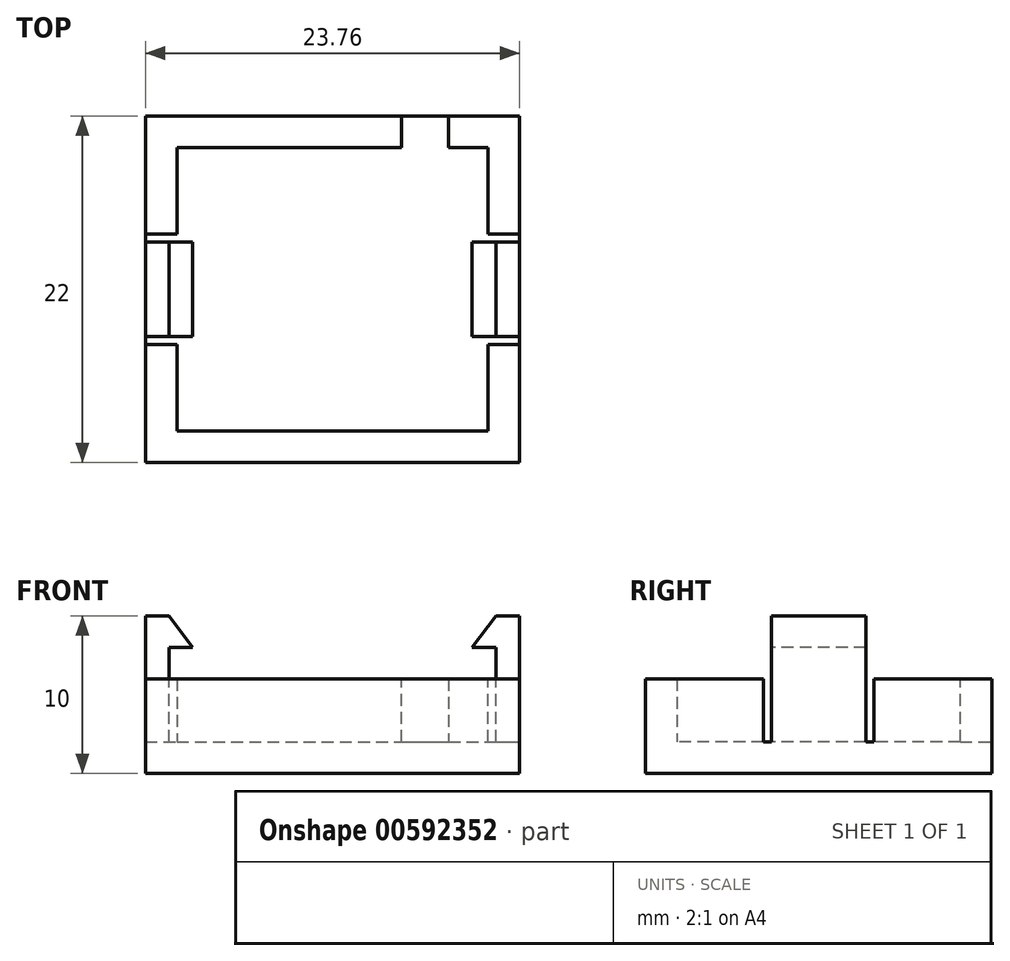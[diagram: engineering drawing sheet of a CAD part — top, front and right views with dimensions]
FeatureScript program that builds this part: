
annotation { "Feature Type Name" : "Feature", "Feature Type Description" : "" }
export const myFeature = defineFeature(function(context is Context, id is Id, definition is map)
    precondition{}
    {
        {
            var Q0;
            Q0=qCreatedBy(makeId("Top.planeOp"),FACE);
            var sketch = newSketch(context, id + "F0", { "sketchPlane" : qUnion([Q0])});
            skLineSegment(sketch, "E0.bottom", {"start": v(9.88, -9) * mm, "end": v(-9.88, -9) * mm});
            skLineSegment(sketch, "E0.top", {"start": v(9.88, 9) * mm, "end": v(-9.88, 9) * mm});
            skLineSegment(sketch, "E0.left", {"start": v(9.88, -9) * mm, "end": v(9.88, 9) * mm});
            skLineSegment(sketch, "E0.right", {"start": v(-9.88, -9) * mm, "end": v(-9.88, 9) * mm});
            skPoint(sketch, "E0.middle", {"position": v(0, 0) * mm});
            skLineSegment(sketch, "E1.bottom", {"start": v(11.88, -11) * mm, "end": v(-11.88, -11) * mm});
            skLineSegment(sketch, "E1.top", {"start": v(11.88, 11) * mm, "end": v(-11.88, 11) * mm});
            skLineSegment(sketch, "E1.left", {"start": v(11.88, -11) * mm, "end": v(11.88, 11) * mm});
            skLineSegment(sketch, "E1.right", {"start": v(-11.88, -11) * mm, "end": v(-11.88, 11) * mm});
            skSolve(sketch);
        }
        {
            var Q0;
            Q0 = qSketchRegion(id + "F0", true);
            var Q1;
            Q1=makeQuery(id+"F0.imprint","IMPRINT",FACE,{"disambiguationData":[TD([[makeQuery(id+"F0.imprint","IMPRINT",EDGE,{"derivedFrom":sQuery(id+"F0.wireOp",EDGE,"E0.bottom")}),-1.0]])]});
            extrude(context, id + "F1", {"entities" : qUnion([Q0, Q1]), "depth" : 2 * mm, "offsetDistance" : 25 * mm});
        }
        {
            var Q0;
            Q0=makeQuery(id+"F0.imprint","IMPRINT",FACE,{"disambiguationData":[TD([[makeQuery(id+"F0.imprint","IMPRINT",EDGE,{"derivedFrom":sQuery(id+"F0.wireOp",EDGE,"E0.bottom")}),1.0]])]});
            extrude(context, id + "F2", {"entities" : qUnion([Q0]), "operationType" : NewBodyOperationType.ADD, "depth" : 6 * mm, "offsetDistance" : 25 * mm});
        }
        {
            var Q0;
            Q0=makeQuery(id+"F2.opExtrude","CAP_FACE",FACE,{"disambiguationData":[OSD([sQuery(id+"F0.wireOp",EDGE,"E0.bottom"),sQuery(id+"F0.wireOp",EDGE,"E0.top"),sQuery(id+"F0.wireOp",EDGE,"E0.left"),sQuery(id+"F0.wireOp",EDGE,"E0.right"),sQuery(id+"F0.wireOp",EDGE,"E1.bottom"),sQuery(id+"F0.wireOp",EDGE,"E1.top"),sQuery(id+"F0.wireOp",EDGE,"E1.left"),sQuery(id+"F0.wireOp",EDGE,"E1.right")])],"isStart":false});
            var sketch = newSketch(context, id + "F3", { "sketchPlane" : qUnion([Q0])});
            skLineSegment(sketch, "E2.bottom", {"start": v(9.88, 3) * mm, "end": v(11.88, 3) * mm});
            skLineSegment(sketch, "E2.top", {"start": v(9.88, -3) * mm, "end": v(11.88, -3) * mm});
            skLineSegment(sketch, "E2.left", {"start": v(9.88, 3) * mm, "end": v(9.88, -3) * mm});
            skLineSegment(sketch, "E2.right", {"start": v(11.88, 3) * mm, "end": v(11.88, -3) * mm});
            skLineSegment(sketch, "E3", {"start": v(9.88, -3.5) * mm, "end": v(11.88, -3.5) * mm});
            skLineSegment(sketch, "E4", {"start": v(9.88, 3.5) * mm, "end": v(11.88, 3.5) * mm});
            skLineSegment(sketch, "E5", {"start": v(11.88, -3.5) * mm, "end": v(11.88, -3) * mm});
            skLineSegment(sketch, "E6", {"start": v(9.88, -3) * mm, "end": v(9.88, -3.5) * mm});
            skLineSegment(sketch, "E7", {"start": v(9.88, 3.5) * mm, "end": v(9.88, 3) * mm});
            skLineSegment(sketch, "E8", {"start": v(11.88, 3.5) * mm, "end": v(11.88, 3) * mm});
            skLineSegment(sketch, "E9.bottom", {"start": v(-11.88, 3) * mm, "end": v(-9.88, 3) * mm});
            skLineSegment(sketch, "E9.top", {"start": v(-11.88, -3) * mm, "end": v(-9.88, -3) * mm});
            skLineSegment(sketch, "E9.left", {"start": v(-11.88, 3) * mm, "end": v(-11.88, -3) * mm});
            skLineSegment(sketch, "E9.right", {"start": v(-9.88, 3) * mm, "end": v(-9.88, -3) * mm});
            skLineSegment(sketch, "E10.top", {"start": v(-11.88, 3.5) * mm, "end": v(-9.88, 3.5) * mm});
            skLineSegment(sketch, "E10.left", {"start": v(-11.88, 3) * mm, "end": v(-11.88, 3.5) * mm});
            skLineSegment(sketch, "E10.right", {"start": v(-9.88, 3) * mm, "end": v(-9.88, 3.5) * mm});
            skLineSegment(sketch, "E11.top", {"start": v(-11.88, -3.5) * mm, "end": v(-9.88, -3.5) * mm});
            skLineSegment(sketch, "E11.left", {"start": v(-11.88, -3) * mm, "end": v(-11.88, -3.5) * mm});
            skLineSegment(sketch, "E11.right", {"start": v(-9.88, -3) * mm, "end": v(-9.88, -3.5) * mm});
            skLineSegment(sketch, "E12.bottom", {"start": v(9.88, 3) * mm, "end": v(10.88, 3) * mm});
            skLineSegment(sketch, "E12.top", {"start": v(9.88, -3) * mm, "end": v(10.88, -3) * mm});
            skLineSegment(sketch, "E12.right", {"start": v(10.88, 3) * mm, "end": v(10.88, -3) * mm});
            skSolve(sketch);
        }
        {
            var Q0;
            Q0=makeQuery(id+"F3.imprint","IMPRINT",FACE,{"disambiguationData":[TD([[makeQuery(id+"F3.imprint","IMPRINT",EDGE,{"derivedFrom":sQuery(id+"F3.wireOp",EDGE,"E2.top")}),-1.0]])]});
            var Q1;
            Q1=makeQuery(id+"F3.imprint","IMPRINT",FACE,{"disambiguationData":[TD([[makeQuery(id+"F3.imprint","IMPRINT",EDGE,{"derivedFrom":sQuery(id+"F3.wireOp",EDGE,"E2.bottom")}),1.0]])]});
            var Q2;
            Q2=makeQuery(id+"F3.imprint","IMPRINT",FACE,{"disambiguationData":[TD([[makeQuery(id+"F3.imprint","IMPRINT",EDGE,{"derivedFrom":sQuery(id+"F3.wireOp",EDGE,"E9.bottom")}),1.0]])]});
            var Q3;
            Q3=makeQuery(id+"F3.imprint","IMPRINT",FACE,{"disambiguationData":[TD([[makeQuery(id+"F3.imprint","IMPRINT",EDGE,{"derivedFrom":sQuery(id+"F3.wireOp",EDGE,"E9.top")}),-1.0]])]});
            extrude(context, id + "F4", {"entities" : qUnion([Q0, Q1, Q2, Q3]), "operationType" : NewBodyOperationType.REMOVE, "oppositeDirection" : true, "depth" : 4 * mm, "offsetDistance" : 25 * mm});
        }
        {
            var Q0;
            {var subQ0=sQuery(id+"F0.wireOp",EDGE,"E0.left");var subQ1=sQuery(id+"F0.wireOp",EDGE,"E1.left");Q0=makeQuery(id+"F4.boolean.opBoolean","SPLIT",FACE,{"disambiguationData":[TD([makeQuery(id+"F4.opExtrude","SWEPT_FACE",FACE,{"disambiguationData":[OSD([sQuery(id+"F3.wireOp",EDGE,"E2.bottom")])]})])],"derivedFrom":makeQuery(id+"F2.opExtrude","CAP_FACE",FACE,{"disambiguationData":[OSD([sQuery(id+"F0.wireOp",EDGE,"E0.bottom"),sQuery(id+"F0.wireOp",EDGE,"E0.top"),subQ0,sQuery(id+"F0.wireOp",EDGE,"E0.right"),sQuery(id+"F0.wireOp",EDGE,"E1.bottom"),sQuery(id+"F0.wireOp",EDGE,"E1.top"),subQ1,sQuery(id+"F0.wireOp",EDGE,"E1.right")])],"isStart":false})});}
            var Q1;
            {var subQ0=sQuery(id+"F0.wireOp",EDGE,"E0.right");var subQ1=sQuery(id+"F0.wireOp",EDGE,"E1.right");Q1=makeQuery(id+"F4.boolean.opBoolean","SPLIT",FACE,{"disambiguationData":[TD([makeQuery(id+"F4.opExtrude","SWEPT_FACE",FACE,{"disambiguationData":[OSD([sQuery(id+"F3.wireOp",EDGE,"E9.bottom")])]})])],"derivedFrom":makeQuery(id+"F2.opExtrude","CAP_FACE",FACE,{"disambiguationData":[OSD([sQuery(id+"F0.wireOp",EDGE,"E0.bottom"),sQuery(id+"F0.wireOp",EDGE,"E0.top"),sQuery(id+"F0.wireOp",EDGE,"E0.left"),subQ0,sQuery(id+"F0.wireOp",EDGE,"E1.bottom"),sQuery(id+"F0.wireOp",EDGE,"E1.top"),sQuery(id+"F0.wireOp",EDGE,"E1.left"),subQ1])],"isStart":false})});}
            extrude(context, id + "F5", {"entities" : qUnion([Q0, Q1]), "operationType" : NewBodyOperationType.ADD, "depth" : 4 * mm, "offsetDistance" : 25 * mm});
        }
        {
            var Q0;
            {var subQ0=sQuery(id+"F3.wireOp",EDGE,"E2.top");Q0=makeQuery(id+"F5.boolean.opBoolean","MERGE",FACE,{"derivedFrom":[makeQuery(id+"F4.boolean.opBoolean","COPY",FACE,{"derivedFrom":makeQuery(id+"F4.opExtrude","SWEPT_FACE",FACE,{"disambiguationData":[OSD([subQ0])]})}),makeQuery(id+"F5.opExtrude","SWEPT_FACE",FACE,{"disambiguationData":[OSD([subQ0])]})]});}
            var sketch = newSketch(context, id + "F6", { "sketchPlane" : qUnion([Q0])});
            skLineSegment(sketch, "E13.bottom", {"start": v(11.88, 10) * mm, "end": v(10.38, 10) * mm});
            skLineSegment(sketch, "E13.top", {"start": v(11.88, 8) * mm, "end": v(10.38, 8) * mm});
            skLineSegment(sketch, "E13.left", {"start": v(11.88, 10) * mm, "end": v(11.88, 8) * mm});
            skLineSegment(sketch, "E13.right", {"start": v(10.38, 10) * mm, "end": v(10.38, 8) * mm});
            skLineSegment(sketch, "E14", {"start": v(10.37, 8) * mm, "end": v(11.87, 10) * mm});
            skLineSegment(sketch, "E15", {"start": v(10.38, 8) * mm, "end": v(-6.12, 8) * mm, "construction": true});
            skSolve(sketch);
        }
        {
            var Q0;
            {var subQ0=sQuery(id+"F6.wireOp",EDGE,"E13.top");Q0=makeQuery(id+"F6.imprint","IMPRINT",FACE,{"disambiguationData":[TD([[makeQuery(id+"F6.imprint","IMPRINT",EDGE,{"derivedFrom":subQ0}),-1.0]])]});}
            var Q1;
            {var subQ0=sQuery(id+"F6.wireOp",EDGE,"9DU1TNyU-t0Yq-bJ8T-y5l7-213zkWhciGSZ.top");Q1=makeQuery(id+"F6.imprint","IMPRINT",FACE,{"disambiguationData":[TD([[makeQuery(id+"F6.imprint","IMPRINT",EDGE,{"derivedFrom":subQ0}),1.0]])]});}
            extrude(context, id + "F7", {"entities" : qUnion([Q0, Q1]), "operationType" : NewBodyOperationType.ADD, "oppositeDirection" : true, "depth" : 6 * mm, "offsetDistance" : 25 * mm});
        }
        {
            var Q0;
            {var subQ0=sQuery(id+"F0.wireOp",EDGE,"E1.top");Q0=makeQuery(id+"F2.boolean.opBoolean","MERGE",FACE,{"derivedFrom":[makeQuery(id+"F1.opExtrude","SWEPT_FACE",FACE,{"disambiguationData":[OSD([subQ0])]}),makeQuery(id+"F2.opExtrude","SWEPT_FACE",FACE,{"disambiguationData":[OSD([subQ0])]})]});}
            var sketch = newSketch(context, id + "F8", { "sketchPlane" : qUnion([Q0])});
            skLineSegment(sketch, "E16.bottom", {"start": v(-4.38, 6) * mm, "end": v(-7.38, 6) * mm});
            skLineSegment(sketch, "E16.top", {"start": v(-4.38, 2) * mm, "end": v(-7.38, 2) * mm});
            skLineSegment(sketch, "E16.left", {"start": v(-4.38, 6) * mm, "end": v(-4.38, 2) * mm});
            skLineSegment(sketch, "E16.right", {"start": v(-7.38, 6) * mm, "end": v(-7.38, 2) * mm});
            skSolve(sketch);
        }
        {
            var Q0;
            Q0=makeQuery(id+"F8.imprint","IMPRINT",FACE,{"disambiguationData":[TD([[makeQuery(id+"F8.imprint","IMPRINT",EDGE,{"derivedFrom":sQuery(id+"F8.wireOp",EDGE,"E16.bottom")}),-1.0]])]});
            extrude(context, id + "F9", {"entities" : qUnion([Q0]), "operationType" : NewBodyOperationType.REMOVE, "oppositeDirection" : true, "depth" : 5.2 * mm, "offsetDistance" : 25 * mm});
        }
        {
            var Q0;
            {var subQ0=sQuery(id+"F0.wireOp",EDGE,"E0.right");var subQ1=sQuery(id+"F0.wireOp",EDGE,"E1.right");var subQ2=sQuery(id+"F0.wireOp",EDGE,"E1.left");var subQ3=sQuery(id+"F0.wireOp",EDGE,"E1.top");var subQ4=sQuery(id+"F0.wireOp",EDGE,"E1.bottom");var subQ5=sQuery(id+"F0.wireOp",EDGE,"E0.left");var subQ6=sQuery(id+"F0.wireOp",EDGE,"E0.top");var subQ7=sQuery(id+"F0.wireOp",EDGE,"E0.bottom");Q0=makeQuery(id+"F5.opExtrude","CAP_FACE",FACE,{"disambiguationData":[OSD([subQ7,subQ6,subQ5,subQ0,subQ4,subQ3,subQ2,subQ1]),TDD([makeQuery(id+"F4.boolean.opBoolean","SPLIT",FACE,{"disambiguationData":[TD([makeQuery(id+"F4.opExtrude","SWEPT_FACE",FACE,{"disambiguationData":[OSD([sQuery(id+"F3.wireOp",EDGE,"E9.bottom")])]})])],"derivedFrom":makeQuery(id+"F2.opExtrude","CAP_FACE",FACE,{"disambiguationData":[OSD([subQ7,subQ6,subQ5,subQ0,subQ4,subQ3,subQ2,subQ1])],"isStart":false})})])],"isStart":false});}
            var sketch = newSketch(context, id + "F10", { "sketchPlane" : qUnion([Q0])});
            skLineSegment(sketch, "E17.bottom", {"start": v(-9.88, 3) * mm, "end": v(-10.38, 3) * mm});
            skLineSegment(sketch, "E17.top", {"start": v(-9.88, -3) * mm, "end": v(-10.37, -3) * mm});
            skLineSegment(sketch, "E17.left", {"start": v(-9.88, 3) * mm, "end": v(-9.88, -3) * mm});
            skLineSegment(sketch, "E17.right", {"start": v(-10.38, 3) * mm, "end": v(-10.37, -3) * mm});
            skSolve(sketch);
        }
        {
            var Q0;
            Q0=makeQuery(id+"F10.imprint","IMPRINT",FACE,{"disambiguationData":[TD([[makeQuery(id+"F10.imprint","IMPRINT",EDGE,{"derivedFrom":sQuery(id+"F10.wireOp",EDGE,"E17.bottom")}),-1.0]])]});
            extrude(context, id + "F11", {"entities" : qUnion([Q0]), "operationType" : NewBodyOperationType.REMOVE, "oppositeDirection" : true, "depth" : 8 * mm, "offsetDistance" : 25 * mm});
        }
        {
            var Q0;
            {var subQ0=sQuery(id+"F0.wireOp",EDGE,"E0.left");var subQ1=sQuery(id+"F0.wireOp",EDGE,"E1.left");var subQ2=sQuery(id+"F0.wireOp",EDGE,"E1.right");var subQ3=sQuery(id+"F0.wireOp",EDGE,"E1.top");var subQ4=sQuery(id+"F0.wireOp",EDGE,"E1.bottom");var subQ5=sQuery(id+"F0.wireOp",EDGE,"E0.right");var subQ6=sQuery(id+"F0.wireOp",EDGE,"E0.top");var subQ7=sQuery(id+"F0.wireOp",EDGE,"E0.bottom");Q0=makeQuery(id+"F5.opExtrude","CAP_FACE",FACE,{"disambiguationData":[OSD([subQ7,subQ6,subQ0,subQ5,subQ4,subQ3,subQ1,subQ2]),TDD([makeQuery(id+"F4.boolean.opBoolean","SPLIT",FACE,{"disambiguationData":[TD([makeQuery(id+"F4.opExtrude","SWEPT_FACE",FACE,{"disambiguationData":[OSD([sQuery(id+"F3.wireOp",EDGE,"E2.bottom"),sQuery(id+"F3.wireOp",EDGE,"E12.bottom")])]})])],"derivedFrom":makeQuery(id+"F2.opExtrude","CAP_FACE",FACE,{"disambiguationData":[OSD([subQ7,subQ6,subQ0,subQ5,subQ4,subQ3,subQ1,subQ2])],"isStart":false})})])],"isStart":false});}
            var sketch = newSketch(context, id + "F12", { "sketchPlane" : qUnion([Q0])});
            skLineSegment(sketch, "E18.bottom", {"start": v(9.88, 3) * mm, "end": v(10.38, 3) * mm});
            skLineSegment(sketch, "E18.top", {"start": v(9.88, -3) * mm, "end": v(10.38, -3) * mm});
            skLineSegment(sketch, "E18.left", {"start": v(9.88, 3) * mm, "end": v(9.88, -3) * mm});
            skLineSegment(sketch, "E18.right", {"start": v(10.38, 3) * mm, "end": v(10.38, -3) * mm});
            skSolve(sketch);
        }
        {
            var Q0;
            Q0=makeQuery(id+"F12.imprint","IMPRINT",FACE,{"disambiguationData":[TD([[makeQuery(id+"F12.imprint","IMPRINT",EDGE,{"derivedFrom":sQuery(id+"F12.wireOp",EDGE,"E18.bottom")}),-1.0]])]});
            extrude(context, id + "F13", {"entities" : qUnion([Q0]), "operationType" : NewBodyOperationType.REMOVE, "oppositeDirection" : true, "depth" : 8 * mm, "offsetDistance" : 25 * mm});
        }
        {
            var Q0;
            {var subQ0=sQuery(id+"F3.wireOp",EDGE,"E12.top");var subQ1=sQuery(id+"F3.wireOp",EDGE,"E2.top");Q0=makeQuery(id+"F5.boolean.opBoolean","MERGE",FACE,{"derivedFrom":[makeQuery(id+"F4.boolean.opBoolean","COPY",FACE,{"derivedFrom":makeQuery(id+"F4.opExtrude","SWEPT_FACE",FACE,{"disambiguationData":[OSD([subQ1,subQ0])]})}),makeQuery(id+"F5.opExtrude","SWEPT_FACE",FACE,{"disambiguationData":[OSD([subQ1,subQ0])]})]});}
            var sketch = newSketch(context, id + "F14", { "sketchPlane" : qUnion([Q0])});
            skLineSegment(sketch, "E19.bottom", {"start": v(10.38, 10) * mm, "end": v(8.88, 10) * mm});
            skLineSegment(sketch, "E19.top", {"start": v(10.38, 8) * mm, "end": v(8.88, 8) * mm});
            skLineSegment(sketch, "E19.left", {"start": v(10.38, 10) * mm, "end": v(10.38, 8) * mm});
            skLineSegment(sketch, "E19.right", {"start": v(8.88, 10) * mm, "end": v(8.88, 8) * mm});
            skLineSegment(sketch, "E20", {"start": v(8.88, 8) * mm, "end": v(10.38, 10) * mm});
            skSolve(sketch);
        }
        {
            var Q0;
            Q0=makeQuery(id+"F14.imprint","IMPRINT",FACE,{"disambiguationData":[TD([[makeQuery(id+"F14.imprint","IMPRINT",EDGE,{"derivedFrom":sQuery(id+"F14.wireOp",EDGE,"E19.top")}),-1.0]])]});
            extrude(context, id + "F15", {"entities" : qUnion([Q0]), "operationType" : NewBodyOperationType.ADD, "oppositeDirection" : true, "depth" : 6 * mm, "offsetDistance" : 25 * mm});
        }
        {
            var Q0;
            {var subQ0=sQuery(id+"F3.wireOp",EDGE,"E9.top");Q0=makeQuery(id+"F5.boolean.opBoolean","MERGE",FACE,{"derivedFrom":[makeQuery(id+"F4.boolean.opBoolean","COPY",FACE,{"derivedFrom":makeQuery(id+"F4.opExtrude","SWEPT_FACE",FACE,{"disambiguationData":[OSD([subQ0])]})}),makeQuery(id+"F5.opExtrude","SWEPT_FACE",FACE,{"disambiguationData":[OSD([subQ0])]})]});}
            var sketch = newSketch(context, id + "F16", { "sketchPlane" : qUnion([Q0])});
            skLineSegment(sketch, "E21.bottom", {"start": v(-10.37, 10) * mm, "end": v(-8.87, 10) * mm});
            skLineSegment(sketch, "E21.top", {"start": v(-10.37, 8) * mm, "end": v(-8.87, 8) * mm});
            skLineSegment(sketch, "E21.left", {"start": v(-10.37, 10) * mm, "end": v(-10.37, 8) * mm});
            skLineSegment(sketch, "E21.right", {"start": v(-8.87, 10) * mm, "end": v(-8.87, 8) * mm});
            skLineSegment(sketch, "E22", {"start": v(-10.37, 10) * mm, "end": v(-8.87, 8) * mm});
            skSolve(sketch);
        }
        {
            var Q0;
            Q0=makeQuery(id+"F16.imprint","IMPRINT",FACE,{"disambiguationData":[TD([[makeQuery(id+"F16.imprint","IMPRINT",EDGE,{"derivedFrom":sQuery(id+"F16.wireOp",EDGE,"E21.top")}),1.0]])]});
            extrude(context, id + "F17", {"entities" : qUnion([Q0]), "operationType" : NewBodyOperationType.ADD, "oppositeDirection" : true, "depth" : 6 * mm, "offsetDistance" : 25 * mm});
        }
    });
